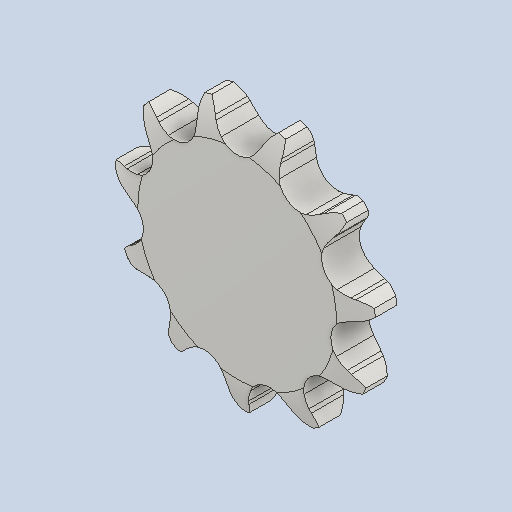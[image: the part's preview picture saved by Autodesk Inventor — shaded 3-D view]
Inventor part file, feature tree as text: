
AUTODESK INVENTOR PART (.ipt)
format: ipt  version: 2022.1 (Build 261234000, 234)  size: 412,672 bytes
history: native  units: mm
features: other x6, extrude x2, pattern_linear x1, pattern_circular x1
ambient origin geometry x8: Origin, YZ Plane, XZ Plane, XY Plane, X Axis, Y Axis, Z Axis, Center Point
bodies: Solid1 (feature_tree)
feature tree (10):
  other  "Perfil de diente teórico"
  other  "Perfil de diente"
  other  "Perfil de sección"
  other  "Cubierta"
  other  "Ramal"
  pattern_linear  "Patrón de ramal"  Spacing1=56.347765mm  [1 undecoded]
  extrude  "Diente teórico"  Depth=5.711987mm
  extrude  "Diente"  Depth=5.1308mm
  pattern_circular  "Patrón de diente"  [2 undecoded]
  other  "Plano síncrono"
note: 3 required parameter values undecoded (feature->parameter linkage not recoverable at this tier; creation-order binding heuristic only, values carry confidence <= 0.55)
